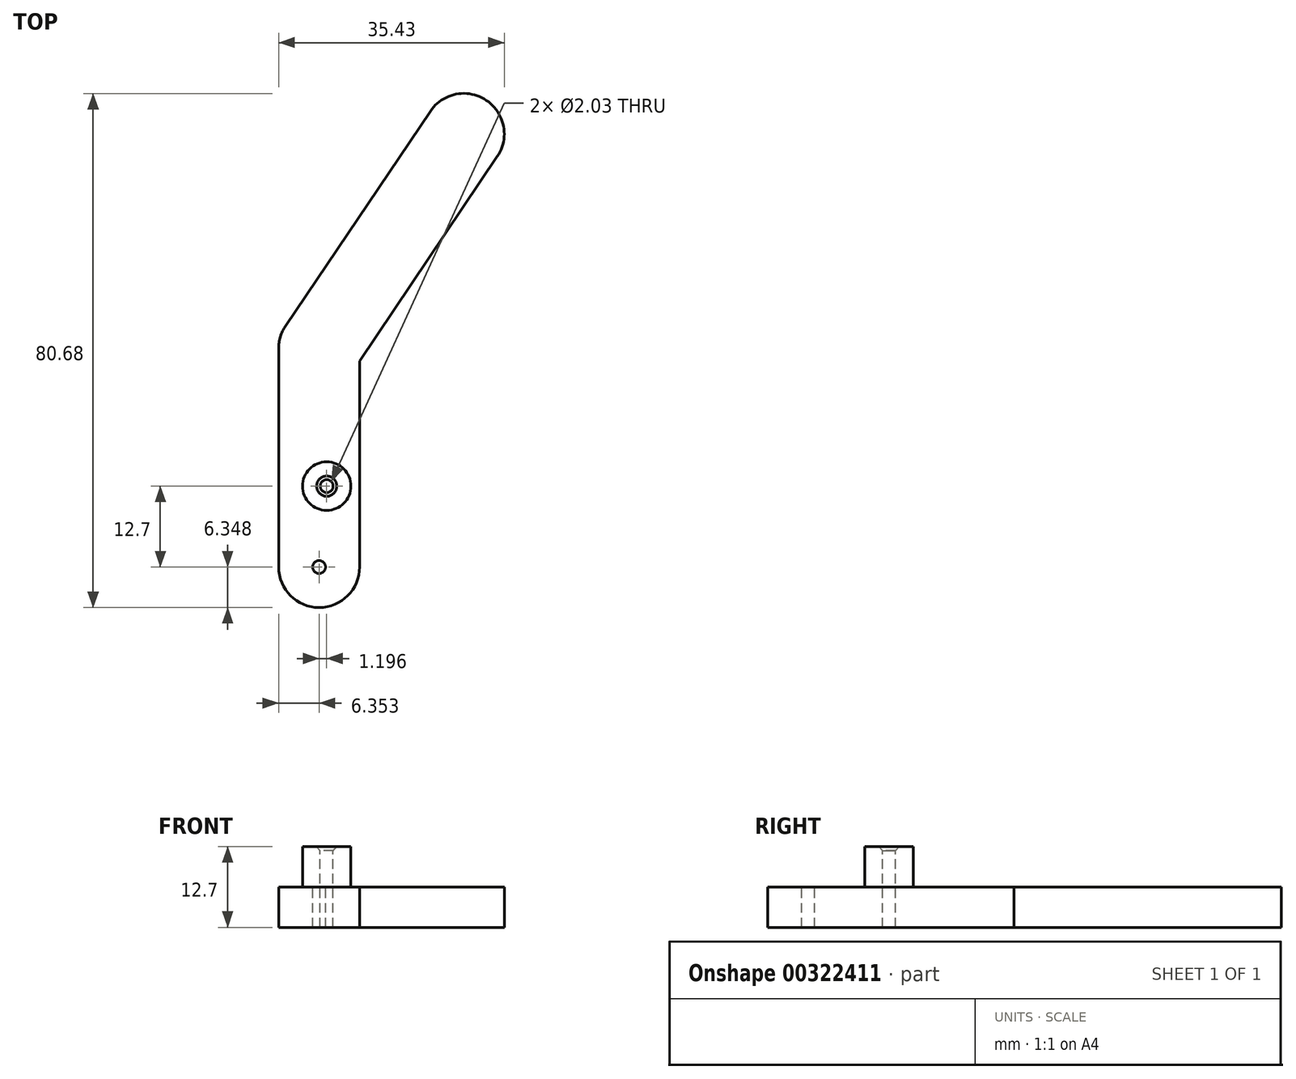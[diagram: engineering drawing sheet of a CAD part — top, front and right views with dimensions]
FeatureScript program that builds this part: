
annotation { "Feature Type Name" : "Feature", "Feature Type Description" : "" }
export const myFeature = defineFeature(function(context is Context, id is Id, definition is map)
    precondition{}
    {
        {
            var Q0;
            Q0=qCreatedBy(makeId("Top.planeOp"),FACE);
            var sketch = newSketch(context, id + "F0", { "sketchPlane" : qUnion([Q0])});
            skLineSegment(sketch, "E0", {"start": v(-106.78, -276.83) * mm, "end": v(-129.5, -310.52) * mm});
            skLineSegment(sketch, "E1", {"start": v(-129.5, -310.52) * mm, "end": v(-129.5, -332.11) * mm});
            skLineSegment(sketch, "E2", {"start": v(-129.5, -332.11) * mm, "end": v(-129.5, -344.81) * mm});
            skArc(sketch, "E3.0.startCap", {"start": v(-135.86, -332.11) * mm, "mid": v(-129.5, -325.76) * mm, "end": v(-123.16, -332.11) * mm});
            skArc(sketch, "E3.0.endCap", {"start": v(-123.16, -344.81) * mm, "mid": v(-129.5, -351.16) * mm, "end": v(-135.86, -344.81) * mm});
            skLineSegment(sketch, "E3.0.left", {"start": v(-123.16, -332.11) * mm, "end": v(-123.16, -344.81) * mm});
            skLineSegment(sketch, "E3.0.right", {"start": v(-135.86, -332.11) * mm, "end": v(-135.86, -344.81) * mm});
            skArc(sketch, "E3.1.startCap", {"start": v(-135.86, -310.52) * mm, "mid": v(-129.5, -304.17) * mm, "end": v(-123.16, -310.52) * mm});
            skArc(sketch, "E3.1.endCap", {"start": v(-123.16, -332.11) * mm, "mid": v(-129.5, -338.46) * mm, "end": v(-135.86, -332.11) * mm});
            skLineSegment(sketch, "E3.1.left", {"start": v(-123.16, -310.52) * mm, "end": v(-123.16, -332.11) * mm});
            skLineSegment(sketch, "E3.1.right", {"start": v(-135.86, -310.52) * mm, "end": v(-135.86, -332.11) * mm});
            skArc(sketch, "E3.2.startCap", {"start": v(-112.05, -273.28) * mm, "mid": v(-103.23, -271.57) * mm, "end": v(-101.52, -280.38) * mm});
            skArc(sketch, "E3.2.endCap", {"start": v(-124.24, -314.07) * mm, "mid": v(-133.06, -315.79) * mm, "end": v(-134.77, -306.97) * mm});
            skLineSegment(sketch, "E3.2.left", {"start": v(-101.52, -280.38) * mm, "end": v(-124.24, -314.07) * mm});
            skLineSegment(sketch, "E3.2.right", {"start": v(-112.05, -273.28) * mm, "end": v(-134.77, -306.97) * mm});
            skSolve(sketch);
        }
        {
            var Q0;
            Q0 = qSketchRegion(id + "F0", true);
            extrude(context, id + "F1", {"entities" : qUnion([Q0]), "depth" : 6.35 * mm});
        }
        {
            var Q0;
            Q0=makeQuery(id+"F1.opExtrude","CAP_FACE",FACE,{"disambiguationData":[OSD([sQuery(id+"F0.wireOp",EDGE,"E3.0.endCap"),sQuery(id+"F0.wireOp",EDGE,"E3.0.left"),sQuery(id+"F0.wireOp",EDGE,"E3.0.right"),sQuery(id+"F0.wireOp",EDGE,"E3.1.left"),sQuery(id+"F0.wireOp",EDGE,"E3.1.right"),sQuery(id+"F0.wireOp",EDGE,"E3.2.startCap"),sQuery(id+"F0.wireOp",EDGE,"E3.2.endCap"),sQuery(id+"F0.wireOp",EDGE,"E3.2.left"),sQuery(id+"F0.wireOp",EDGE,"E3.2.right")])],"isStart":false});
            var sketch = newSketch(context, id + "F2", { "sketchPlane" : qUnion([Q0])});
            skCircle(sketch, "E4", {"center": v(-128.31, -332.11) * mm, "radius": 3.81 * mm});
            skSolve(sketch);
        }
        {
            var Q0;
            Q0 = qSketchRegion(id + "F2", true);
            extrude(context, id + "F3", {"entities" : qUnion([Q0]), "operationType" : NewBodyOperationType.ADD, "depth" : 6.35 * mm});
        }
        {
            var Q0;
            Q0=makeQuery(id+"F3.opExtrude","CAP_FACE",FACE,{"disambiguationData":[OSD([sQuery(id+"F2.wireOp",EDGE,"E4")])],"isStart":false});
            var sketch = newSketch(context, id + "F4", { "sketchPlane" : qUnion([Q0])});
            skPoint(sketch, "E5", {"position": v(-128.31, -332.11) * mm});
            skSolve(sketch);
        }
        {
            var Q0;
            Q0=sQuery(id+"F4.wireOp",VERTEX,"E5");
            var Q1;
            Q1=makeQuery(id+"F1.opExtrude","SWEPT_BODY",BODY,{"disambiguationData":[OSD([sQuery(id+"F0.wireOp",EDGE,"E3.0.endCap"),sQuery(id+"F0.wireOp",EDGE,"E3.0.left"),sQuery(id+"F0.wireOp",EDGE,"E3.0.right"),sQuery(id+"F0.wireOp",EDGE,"E3.1.left"),sQuery(id+"F0.wireOp",EDGE,"E3.1.right"),sQuery(id+"F0.wireOp",EDGE,"E3.2.startCap"),sQuery(id+"F0.wireOp",EDGE,"E3.2.endCap"),sQuery(id+"F0.wireOp",EDGE,"E3.2.left"),sQuery(id+"F0.wireOp",EDGE,"E3.2.right")])]});
            hole(context, id + "F5", {"style" : HoleStyle.C_SINK, "endStyle" : HoleEndStyle.THROUGH, "holeDiameter" : 2.03 * mm, "cSinkDiameter" : 3.17 * mm, "cSinkAngle" : 82 * degree, "tappedDepth" : 12.7 * mm, "tapClearance" : 3, "locations" : qUnion([Q0]), "scope" : qUnion([Q1])});
        }
        {
            var Q0;
            Q0=makeQuery(id+"F1.opExtrude","CAP_FACE",FACE,{"disambiguationData":[OSD([sQuery(id+"F0.wireOp",EDGE,"E3.0.endCap"),sQuery(id+"F0.wireOp",EDGE,"E3.0.left"),sQuery(id+"F0.wireOp",EDGE,"E3.0.right"),sQuery(id+"F0.wireOp",EDGE,"E3.1.left"),sQuery(id+"F0.wireOp",EDGE,"E3.1.right"),sQuery(id+"F0.wireOp",EDGE,"E3.2.startCap"),sQuery(id+"F0.wireOp",EDGE,"E3.2.endCap"),sQuery(id+"F0.wireOp",EDGE,"E3.2.left"),sQuery(id+"F0.wireOp",EDGE,"E3.2.right")])],"isStart":false});
            var sketch = newSketch(context, id + "F6", { "sketchPlane" : qUnion([Q0])});
            skCircle(sketch, "E6", {"center": v(-129.5, -344.81) * mm, "radius": 1.02 * mm});
            skSolve(sketch);
        }
        {
            var Q0;
            Q0=sQuery(id+"F6.wireOp",VERTEX,"E6.center");
            var Q1;
            Q1=makeQuery(id+"F1.opExtrude","SWEPT_BODY",BODY,{"disambiguationData":[OSD([sQuery(id+"F0.wireOp",EDGE,"E3.0.endCap"),sQuery(id+"F0.wireOp",EDGE,"E3.0.left"),sQuery(id+"F0.wireOp",EDGE,"E3.0.right"),sQuery(id+"F0.wireOp",EDGE,"E3.1.left"),sQuery(id+"F0.wireOp",EDGE,"E3.1.right"),sQuery(id+"F0.wireOp",EDGE,"E3.2.startCap"),sQuery(id+"F0.wireOp",EDGE,"E3.2.endCap"),sQuery(id+"F0.wireOp",EDGE,"E3.2.left"),sQuery(id+"F0.wireOp",EDGE,"E3.2.right")])]});
            hole(context, id + "F7", {"style" : HoleStyle.SIMPLE, "endStyle" : HoleEndStyle.THROUGH, "holeDiameter" : 2.03 * mm, "tappedDepth" : 12.7 * mm, "tapClearance" : 3, "locations" : qUnion([Q0]), "scope" : qUnion([Q1])});
        }
    });
